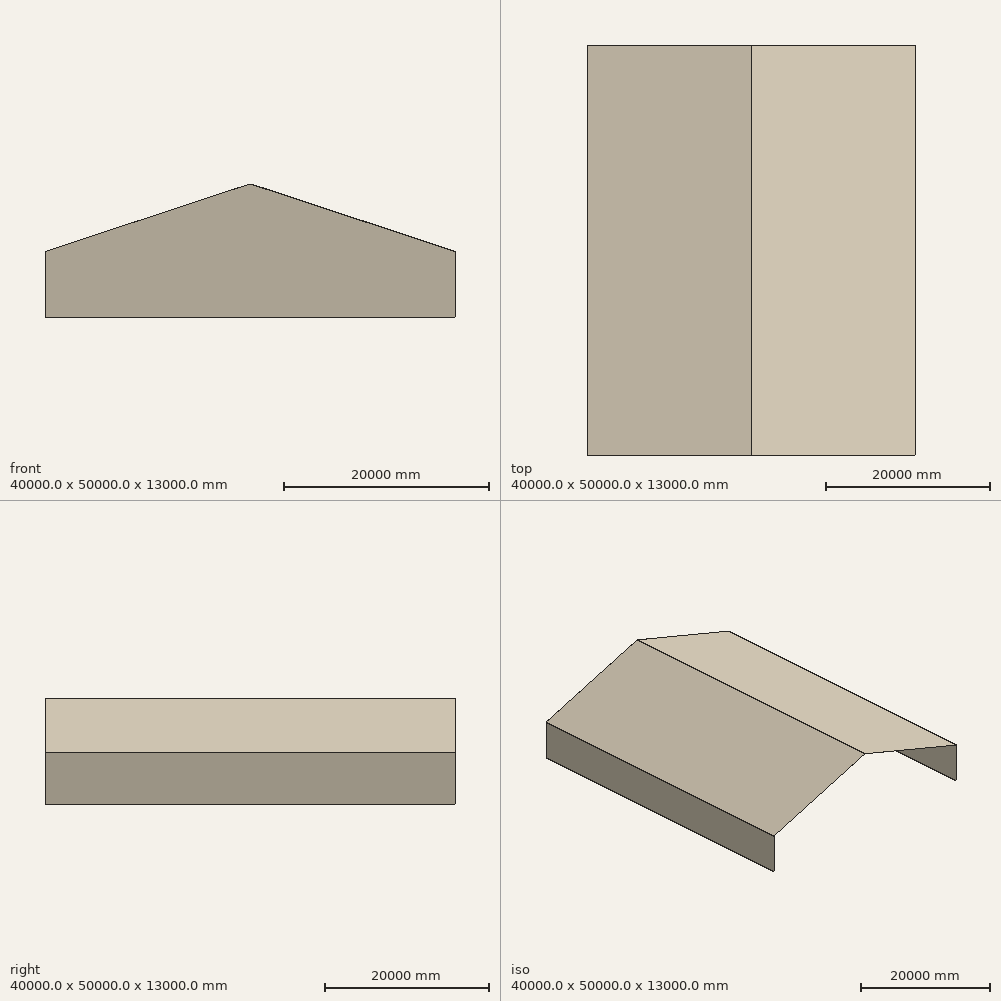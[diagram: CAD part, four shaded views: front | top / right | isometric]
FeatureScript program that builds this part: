
annotation { "Feature Type Name" : "Feature", "Feature Type Description" : "" }
export const myFeature = defineFeature(function(context is Context, id is Id, definition is map)
    precondition{}
    {
        {
            var Q0;
            Q0=qCreatedBy(makeId("Front.planeOp"),FACE);
            var sketch = newSketch(context, id + "F0", { "sketchPlane" : qUnion([Q0])});
            skLineSegment(sketch, "E0", {"start": v(0, 0) * mm, "end": v(0, 13000) * mm, "construction": true});
            skLineSegment(sketch, "E1", {"start": v(0, 13000) * mm, "end": v(-20000, 6400) * mm});
            skLineSegment(sketch, "E2", {"start": v(-20000, 6400) * mm, "end": v(-20000, 0) * mm});
            skLineSegment(sketch, "E3.MirrorCS", {"start": v(0, 13000) * mm, "end": v(20000, 6400) * mm});
            skLineSegment(sketch, "E4.MirrorCS", {"start": v(20000, 6400) * mm, "end": v(20000, 0) * mm});
            skSolve(sketch);
        }
        {
            var Q0;
            Q0=qCreatedBy(makeId("Front.planeOp"),FACE);
            var sketch = newSketch(context, id + "F1", { "sketchPlane" : qUnion([Q0])});
            skLineSegment(sketch, "E5.1", {"start": v(0, 13000) * mm, "end": v(-20000, 6400) * mm});
            skLineSegment(sketch, "E5.2", {"start": v(-20000, 6400) * mm, "end": v(-20000, 0) * mm});
            skLineSegment(sketch, "E5.3", {"start": v(0, 13000) * mm, "end": v(20000, 6400) * mm});
            skLineSegment(sketch, "E5.4", {"start": v(20000, 6400) * mm, "end": v(20000, 0) * mm});
            skLineSegment(sketch, "E6.0", {"start": v(-19999, 6399.28) * mm, "end": v(-19999, 0) * mm});
            skLineSegment(sketch, "E6.1", {"start": v(0, 12998.95) * mm, "end": v(-19999, 6399.28) * mm});
            skLineSegment(sketch, "E6.2", {"start": v(0, 12998.95) * mm, "end": v(19999, 6399.28) * mm});
            skLineSegment(sketch, "E6.3", {"start": v(19999, 6399.28) * mm, "end": v(19999, 0) * mm});
            skLineSegment(sketch, "E7", {"start": v(-19999, 0) * mm, "end": v(-20000, 0) * mm});
            skLineSegment(sketch, "E8", {"start": v(20000, 0) * mm, "end": v(19999, 0) * mm});
            skSolve(sketch);
        }
        {
            var Q0;
            Q0 = qSketchRegion(id + "F1", true);
            extrude(context, id + "F2", {"entities" : qUnion([Q0]), "depth" : 50000 * mm});
        }
        {
            var Q0;
            Q0=qCreatedBy(makeId("Front.planeOp"),FACE);
            var sketch = newSketch(context, id + "F3", { "sketchPlane" : qUnion([Q0])});
            skLineSegment(sketch, "E9.1", {"start": v(0, 13000) * mm, "end": v(-20000, 6400) * mm});
            skLineSegment(sketch, "E9.2", {"start": v(-20000, 6400) * mm, "end": v(-20000, 0) * mm});
            skLineSegment(sketch, "E9.3", {"start": v(0, 13000) * mm, "end": v(20000, 6400) * mm});
            skLineSegment(sketch, "E9.4", {"start": v(20000, 6400) * mm, "end": v(20000, 0) * mm});
            skLineSegment(sketch, "E10", {"start": v(-20000, 0) * mm, "end": v(20000, 0) * mm});
            skSolve(sketch);
        }
        {
            var Q0;
            Q0 = qSketchRegion(id + "F3", true);
            extrude(context, id + "F4", {"entities" : qUnion([Q0]), "depth" : 10 * mm});
        }
    });
